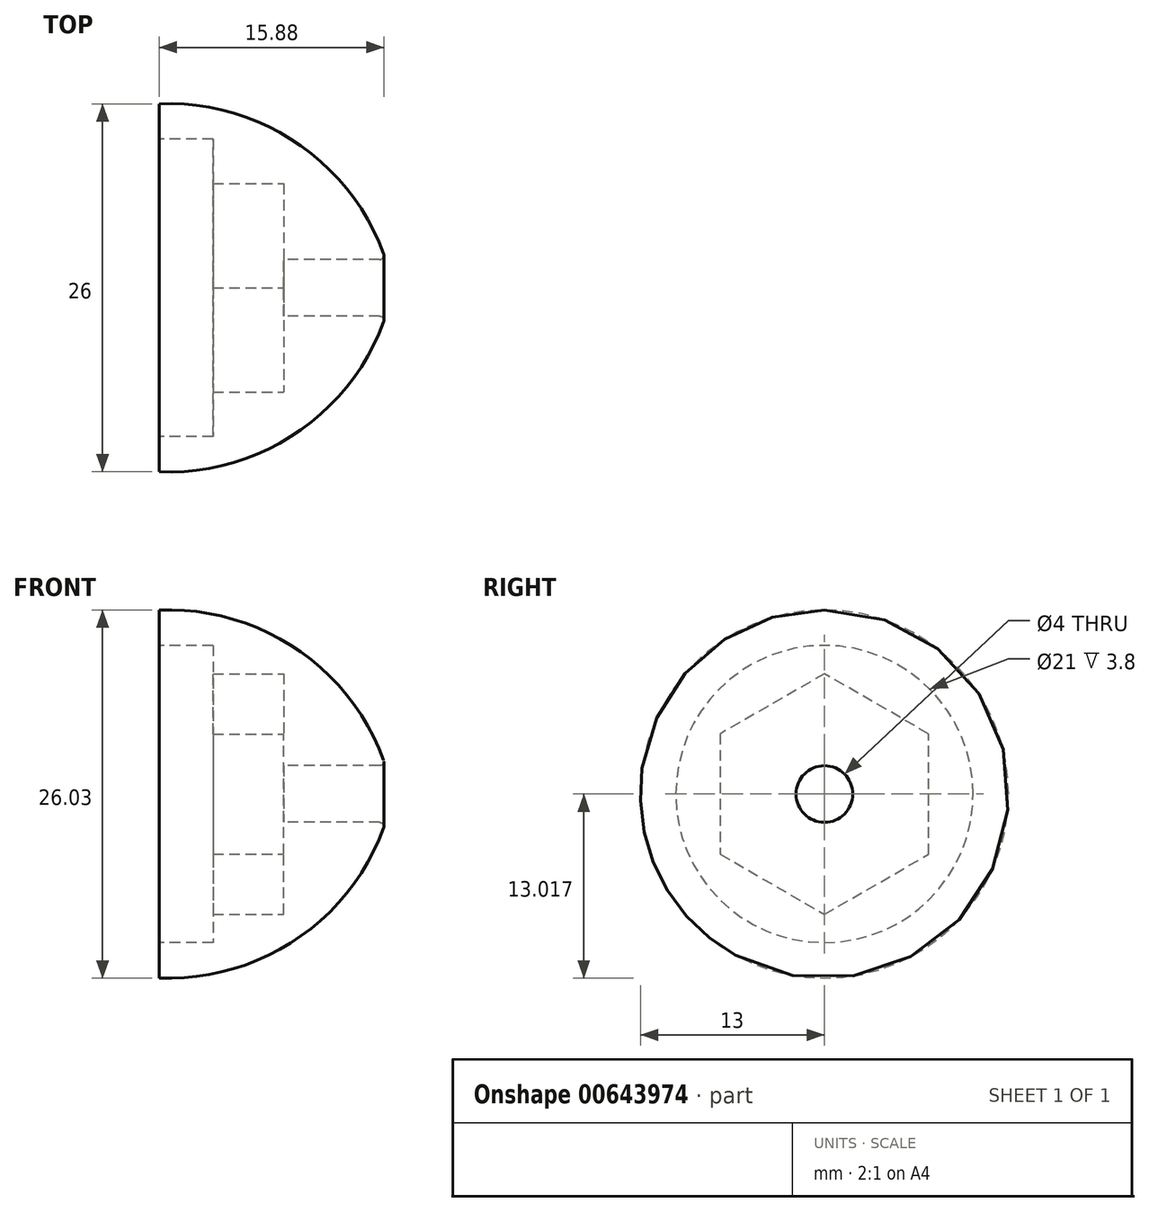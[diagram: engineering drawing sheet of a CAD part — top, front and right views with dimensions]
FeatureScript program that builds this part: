
annotation { "Feature Type Name" : "Feature", "Feature Type Description" : "" }
export const myFeature = defineFeature(function(context is Context, id is Id, definition is map)
    precondition{}
    {
        {
            var Q0;
            Q0=qCreatedBy(makeId("Front.planeOp"),FACE);
            var sketch = newSketch(context, id + "F0", { "sketchPlane" : qUnion([Q0])});
            skLineSegment(sketch, "E0", {"start": v(51.77, -16.47) * mm, "end": v(44.57, -16.47) * mm});
            skLineSegment(sketch, "E1", {"start": v(44.57, -16.47) * mm, "end": v(44.57, -9.97) * mm});
            skLineSegment(sketch, "E2", {"start": v(44.57, -9.97) * mm, "end": v(39.57, -9.97) * mm});
            skLineSegment(sketch, "E3", {"start": v(39.57, -9.97) * mm, "end": v(39.57, -7.97) * mm});
            skLineSegment(sketch, "E4", {"start": v(39.57, -7.97) * mm, "end": v(35.77, -7.97) * mm});
            skLineSegment(sketch, "E5", {"start": v(35.77, -7.97) * mm, "end": v(35.77, -5.47) * mm});
            skArc(sketch, "E6", {"start": v(51.77, -16.47) * mm, "mid": v(45.6, -8.3) * mm, "end": v(35.77, -5.47) * mm});
            skLineSegment(sketch, "E7", {"start": v(37.31, -18.47) * mm, "end": v(53.76, -18.47) * mm, "construction": true});
            skSolve(sketch);
        }
        {
            var Q0;
            Q0=makeQuery(id+"F0.imprint","IMPRINT",FACE,{"disambiguationData":[TD([[makeQuery(id+"F0.imprint","IMPRINT",EDGE,{"derivedFrom":sQuery(id+"F0.wireOp",EDGE,"E0")}),-1.0]])]});
            var Q1;
            Q1=sQuery(id+"F0.wireOp",EDGE,"E7");
            revolve(context, id + "F1", {"entities" : qUnion([Q0]), "axis" : qUnion([Q1]), "revolveType" : RevolveType.FULL});
        }
        {
            var Q0;
            Q0=makeQuery(id+"F1.opRevolve","SWEPT_EDGE",EDGE,{"disambiguationData":[OSD([sQuery(id+"F0.wireOp",EDGE,"E0"),sQuery(id+"F0.wireOp",EDGE,"E6")])]});
            fillet(context, id + "F2", {"entities" : qUnion([Q0]), "radius" : 0.3 * mm, "tangentPropagation" : true, "allowEdgeOverflow" : false});
        }
        {
            var Q0;
            Q0=makeQuery(id+"F1.opRevolve","SWEPT_FACE",FACE,{"disambiguationData":[OSD([sQuery(id+"F0.wireOp",EDGE,"E1")])]});
            var sketch = newSketch(context, id + "F3", { "sketchPlane" : qUnion([Q0])});
            skCircle(sketch, "E8.cCircle", {"center": v(0, -18.47) * mm, "radius": 8.5 * mm});
            skLineSegment(sketch, "E8.0", {"start": v(0, -9.97) * mm, "end": v(7.36, -14.22) * mm});
            skLineSegment(sketch, "E8.1", {"start": v(7.36, -14.22) * mm, "end": v(7.36, -22.72) * mm});
            skLineSegment(sketch, "E8.2", {"start": v(7.36, -22.72) * mm, "end": v(0, -26.97) * mm});
            skLineSegment(sketch, "E8.3", {"start": v(0, -26.97) * mm, "end": v(-7.36, -22.72) * mm});
            skLineSegment(sketch, "E8.4", {"start": v(-7.36, -22.72) * mm, "end": v(-7.36, -14.22) * mm});
            skLineSegment(sketch, "E8.5", {"start": v(-7.36, -14.22) * mm, "end": v(0, -9.97) * mm});
            skSolve(sketch);
        }
        {
            var Q0;
            {var subQ0=sQuery(id+"F3.wireOp",EDGE,"E8.0");Q0=makeQuery(id+"F3.imprint","IMPRINT",FACE,{"disambiguationData":[TD([[makeQuery(id+"F3.imprint","IMPRINT",EDGE,{"derivedFrom":subQ0}),1.0]])]});}
            var Q1;
            {var subQ0=sQuery(id+"F3.wireOp",EDGE,"E8.5");Q1=makeQuery(id+"F3.imprint","IMPRINT",FACE,{"disambiguationData":[TD([[makeQuery(id+"F3.imprint","IMPRINT",EDGE,{"derivedFrom":subQ0}),1.0]])]});}
            var Q2;
            {var subQ0=sQuery(id+"F3.wireOp",EDGE,"E8.4");Q2=makeQuery(id+"F3.imprint","IMPRINT",FACE,{"disambiguationData":[TD([[makeQuery(id+"F3.imprint","IMPRINT",EDGE,{"derivedFrom":subQ0}),1.0]])]});}
            var Q3;
            {var subQ0=sQuery(id+"F3.wireOp",EDGE,"E8.3");Q3=makeQuery(id+"F3.imprint","IMPRINT",FACE,{"disambiguationData":[TD([[makeQuery(id+"F3.imprint","IMPRINT",EDGE,{"derivedFrom":subQ0}),1.0]])]});}
            var Q4;
            {var subQ0=sQuery(id+"F3.wireOp",EDGE,"E8.2");Q4=makeQuery(id+"F3.imprint","IMPRINT",FACE,{"disambiguationData":[TD([[makeQuery(id+"F3.imprint","IMPRINT",EDGE,{"derivedFrom":subQ0}),1.0]])]});}
            var Q5;
            {var subQ0=sQuery(id+"F3.wireOp",EDGE,"E8.1");Q5=makeQuery(id+"F3.imprint","IMPRINT",FACE,{"disambiguationData":[TD([[makeQuery(id+"F3.imprint","IMPRINT",EDGE,{"derivedFrom":subQ0}),1.0]])]});}
            extrude(context, id + "F4", {"entities" : qUnion([Q0, Q1, Q2, Q3, Q4, Q5]), "operationType" : NewBodyOperationType.ADD, "depth" : 5 * mm, "offsetDistance" : 25 * mm});
        }
    });
